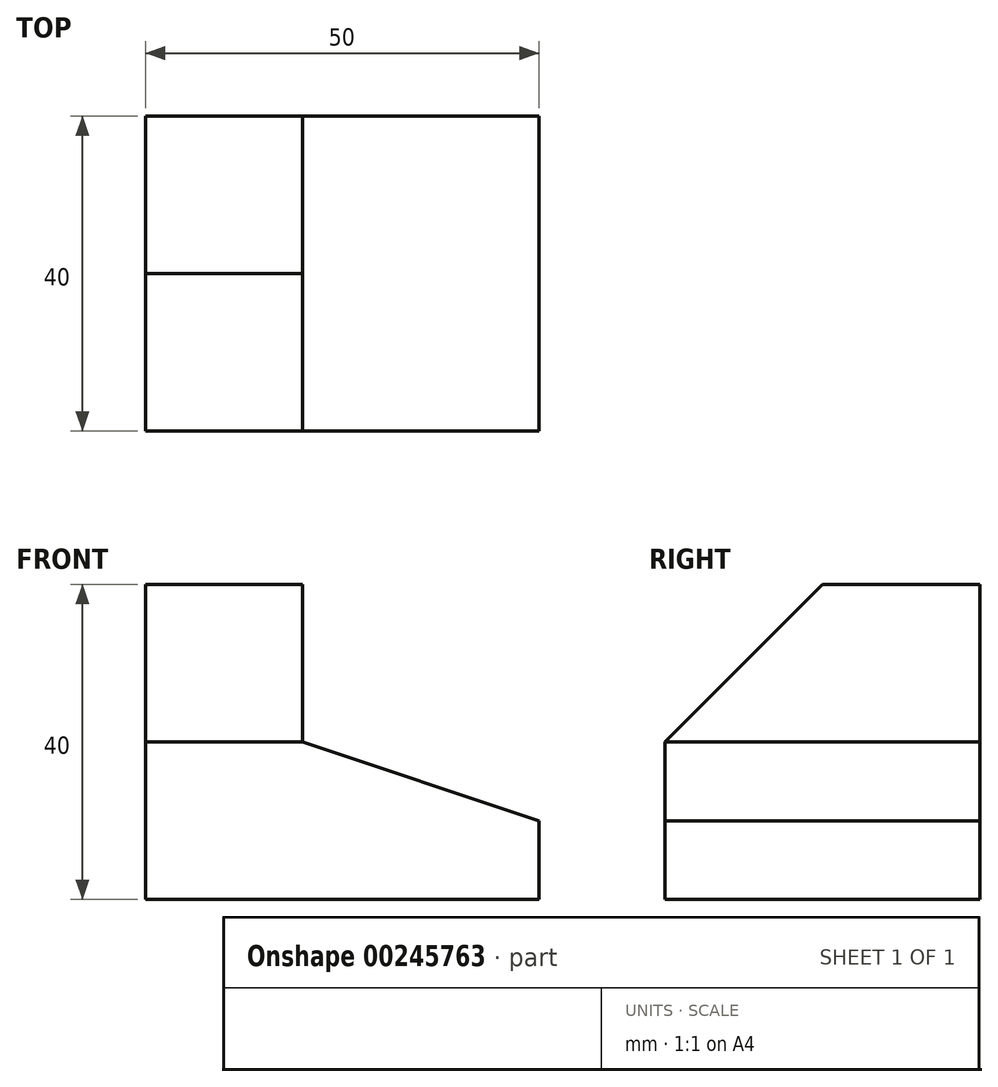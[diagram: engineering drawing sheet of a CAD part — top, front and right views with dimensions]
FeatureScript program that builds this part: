
annotation { "Feature Type Name" : "Feature", "Feature Type Description" : "" }
export const myFeature = defineFeature(function(context is Context, id is Id, definition is map)
    precondition{}
    {
        {
            var Q0;
            Q0=qCreatedBy(makeId("Front.planeOp"),FACE);
            var sketch = newSketch(context, id + "F0", { "sketchPlane" : qUnion([Q0])});
            skLineSegment(sketch, "E0", {"start": v(0, 0) * mm, "end": v(50, 0) * mm});
            skLineSegment(sketch, "E1", {"start": v(0, 0) * mm, "end": v(0, 20) * mm});
            skLineSegment(sketch, "E2", {"start": v(50, 0) * mm, "end": v(50, 10) * mm});
            skLineSegment(sketch, "E3", {"start": v(0, 20) * mm, "end": v(20, 20) * mm});
            skLineSegment(sketch, "E4", {"start": v(20, 20) * mm, "end": v(50, 10) * mm});
            skLineSegment(sketch, "E5", {"start": v(0, 20) * mm, "end": v(0, 40) * mm});
            skLineSegment(sketch, "E6", {"start": v(0, 40) * mm, "end": v(20, 40) * mm});
            skLineSegment(sketch, "E7", {"start": v(20, 40) * mm, "end": v(20, 20) * mm});
            skSolve(sketch);
        }
        {
            var Q0;
            Q0=makeQuery(id+"F0.imprint","IMPRINT",FACE,{"disambiguationData":[TD([[makeQuery(id+"F0.imprint","IMPRINT",EDGE,{"derivedFrom":sQuery(id+"F0.wireOp",EDGE,"E0")}),1.0]])]});
            extrude(context, id + "F1", {"entities" : qUnion([Q0]), "depth" : 40 * mm});
        }
        {
            var Q0;
            Q0=makeQuery(id+"F0.imprint","IMPRINT",FACE,{"disambiguationData":[TD([[makeQuery(id+"F0.imprint","IMPRINT",EDGE,{"derivedFrom":sQuery(id+"F0.wireOp",EDGE,"E3")}),1.0]])]});
            extrude(context, id + "F2", {"entities" : qUnion([Q0]), "operationType" : NewBodyOperationType.ADD, "depth" : 40 * mm});
        }
        {
            var Q0;
            Q0=makeQuery(id+"F2.opExtrude","SWEPT_FACE",FACE,{"disambiguationData":[OSD([sQuery(id+"F0.wireOp",EDGE,"E7")])]});
            var sketch = newSketch(context, id + "F3", { "sketchPlane" : qUnion([Q0])});
            skLineSegment(sketch, "E8", {"start": v(-20, 40) * mm, "end": v(-40, 20) * mm});
            skLineSegment(sketch, "E9", {"start": v(-20, 40) * mm, "end": v(-40, 40) * mm});
            skLineSegment(sketch, "E10", {"start": v(-40, 40) * mm, "end": v(-40, 20) * mm});
            skSolve(sketch);
        }
        {
            var Q0;
            Q0=makeQuery(id+"F3.imprint","IMPRINT",FACE,{"disambiguationData":[TD([[makeQuery(id+"F3.imprint","IMPRINT",EDGE,{"derivedFrom":sQuery(id+"F3.wireOp",EDGE,"E8")}),-1.0]])]});
            extrude(context, id + "F4", {"entities" : qUnion([Q0]), "operationType" : NewBodyOperationType.REMOVE, "oppositeDirection" : true, "depth" : 20 * mm});
        }
    });
